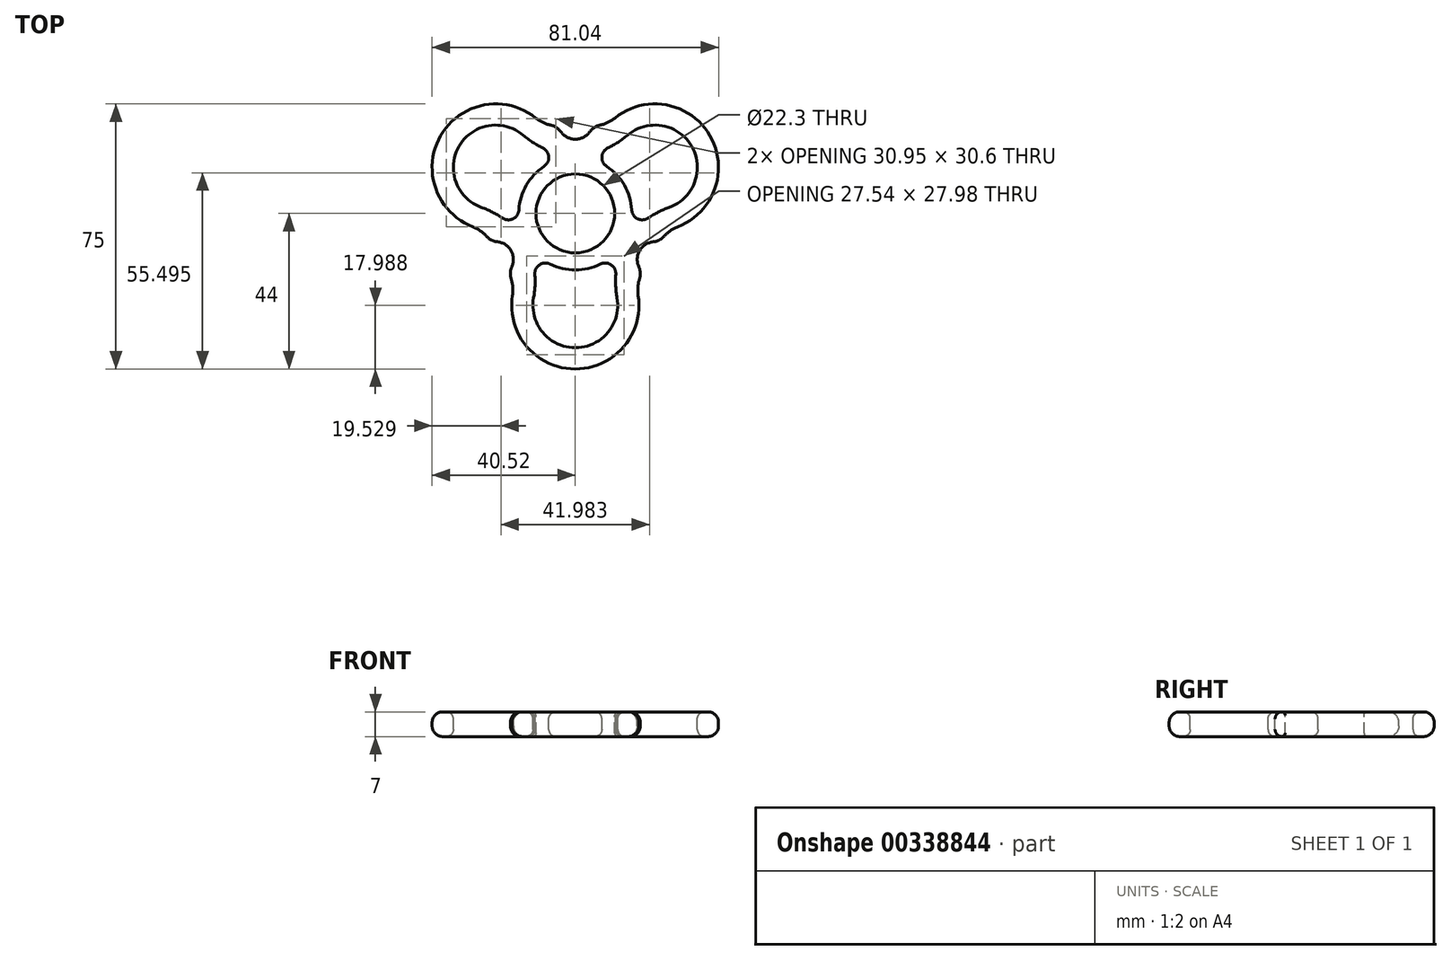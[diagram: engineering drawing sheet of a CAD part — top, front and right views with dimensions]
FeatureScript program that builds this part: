
annotation { "Feature Type Name" : "Feature", "Feature Type Description" : "" }
export const myFeature = defineFeature(function(context is Context, id is Id, definition is map)
    precondition{}
    {
        {
            var Q0;
            Q0=qCreatedBy(makeId("Top.planeOp"),FACE);
            var sketch = newSketch(context, id + "F0", { "sketchPlane" : qUnion([Q0])});
            skCircle(sketch, "E0.cCircle", {"center": v(0, 0) * mm, "radius": 22 * mm, "construction": true});
            skLineSegment(sketch, "E0.0", {"start": v(-38.1, 22) * mm, "end": v(38.1, 22) * mm});
            skLineSegment(sketch, "E0.1", {"start": v(38.1, 22) * mm, "end": v(0, -44) * mm});
            skLineSegment(sketch, "E0.2", {"start": v(0, -44) * mm, "end": v(-38.1, 22) * mm});
            skPoint(sketch, "E0.0.midPoint", {"position": v(0, 22) * mm});
            skLineSegment(sketch, "E1", {"start": v(-38.1, 22) * mm, "end": v(0, 26) * mm});
            skLineSegment(sketch, "E2", {"start": v(0, 26) * mm, "end": v(38.1, 22) * mm});
            skLineSegment(sketch, "E3.1.0", {"start": v(0, -44) * mm, "end": v(-22.52, -13) * mm});
            skLineSegment(sketch, "E3.1.1", {"start": v(-22.52, -13) * mm, "end": v(-38.1, 22) * mm});
            skLineSegment(sketch, "E3.2.0", {"start": v(38.1, 22) * mm, "end": v(22.52, -13) * mm});
            skLineSegment(sketch, "E3.2.1", {"start": v(22.52, -13) * mm, "end": v(0, -44) * mm});
            skSolve(sketch);
        }
        {
            var Q0;
            Q0=qSketchRegion(id+"F0",true);
            extrude(context, id + "F1", {"entities" : qUnion([Q0]), "depth" : 7 * mm});
        }
        {
            var Q0;
            Q0=makeQuery(id+"F1.opExtrude","CAP_FACE",FACE,{"disambiguationData":[OSD([sQuery(id+"F0.wireOp",EDGE,"E1"),sQuery(id+"F0.wireOp",EDGE,"E2"),sQuery(id+"F0.wireOp",EDGE,"E3.1.0"),sQuery(id+"F0.wireOp",EDGE,"E3.1.1"),sQuery(id+"F0.wireOp",EDGE,"E3.2.0"),sQuery(id+"F0.wireOp",EDGE,"E3.2.1")])],"isStart":true});
            var sketch = newSketch(context, id + "F2", { "sketchPlane" : qUnion([Q0])});
            skCircle(sketch, "E4", {"center": v(0, 0) * mm, "radius": 26 * mm, "construction": true});
            skLineSegment(sketch, "E5", {"start": v(0, 0) * mm, "end": v(-38.1, -22) * mm, "construction": true});
            skLineSegment(sketch, "E6", {"start": v(0, 0) * mm, "end": v(38.1, -22) * mm, "construction": true});
            skLineSegment(sketch, "E7", {"start": v(0, 0) * mm, "end": v(0, 44) * mm, "construction": true});
            skCircle(sketch, "E8", {"center": v(-22.52, -13) * mm, "radius": 18 * mm});
            skCircle(sketch, "E9", {"center": v(22.52, -13) * mm, "radius": 18 * mm});
            skCircle(sketch, "E10", {"center": v(0, 26) * mm, "radius": 18 * mm});
            skSolve(sketch);
        }
        {
            var Q0;
            Q0 = qSketchRegion(id + "F2", true);
            extrude(context, id + "F3", {"entities" : qUnion([Q0]), "operationType" : NewBodyOperationType.ADD, "oppositeDirection" : true, "depth" : 7 * mm});
        }
        {
            var Q0;
            Q0=makeQuery(id+"F1.opExtrude","CAP_FACE",FACE,{"disambiguationData":[OSD([sQuery(id+"F0.wireOp",EDGE,"E1"),sQuery(id+"F0.wireOp",EDGE,"E2"),sQuery(id+"F0.wireOp",EDGE,"E3.1.0"),sQuery(id+"F0.wireOp",EDGE,"E3.1.1"),sQuery(id+"F0.wireOp",EDGE,"E3.2.0"),sQuery(id+"F0.wireOp",EDGE,"E3.2.1")])],"isStart":false});
            var sketch = newSketch(context, id + "F4", { "sketchPlane" : qUnion([Q0])});
            skCircle(sketch, "E11", {"center": v(0, 0) * mm, "radius": 11.15 * mm});
            skSolve(sketch);
        }
        {
            var Q0;
            Q0=qSketchRegion(id+"F4",true);
            extrude(context, id + "F5", {"entities" : qUnion([Q0]), "operationType" : NewBodyOperationType.REMOVE, "endBound" : BoundingType.THROUGH_ALL, "oppositeDirection" : true, "depth" : 25 * mm});
        }
        {
            var Q0;
            Q0=makeQuery(id+"F1.opExtrude","CAP_FACE",FACE,{"disambiguationData":[OSD([sQuery(id+"F0.wireOp",EDGE,"E1"),sQuery(id+"F0.wireOp",EDGE,"E2"),sQuery(id+"F0.wireOp",EDGE,"E3.1.0"),sQuery(id+"F0.wireOp",EDGE,"E3.1.1"),sQuery(id+"F0.wireOp",EDGE,"E3.2.0"),sQuery(id+"F0.wireOp",EDGE,"E3.2.1")])],"isStart":false});
            var sketch = newSketch(context, id + "F6", { "sketchPlane" : qUnion([Q0])});
            skArc(sketch, "E12", {"start": v(-4.05, 23.06) * mm, "mid": v(0, 21) * mm, "end": v(4.05, 23.06) * mm});
            skLineSegment(sketch, "E13", {"start": v(-31.26, 22.72) * mm, "end": v(-8.61, 25.1) * mm});
            skLineSegment(sketch, "E14", {"start": v(8.61, 25.1) * mm, "end": v(31.26, 22.72) * mm});
            skPoint(sketch, "E15.visualSharp", {"position": v(-4.97, 25.48) * mm});
            skArc(sketch, "E15.filletArc", {"start": v(-4.05, 23.06) * mm, "mid": v(-6.06, 24.7) * mm, "end": v(-8.61, 25.1) * mm});
            skPoint(sketch, "E16.visualSharp", {"position": v(4.97, 25.48) * mm});
            skArc(sketch, "E16.filletArc", {"start": v(8.61, 25.1) * mm, "mid": v(6.06, 24.7) * mm, "end": v(4.05, 23.06) * mm});
            skLineSegment(sketch, "E17", {"start": v(-8.61, 25.1) * mm, "end": v(0, 26) * mm});
            skLineSegment(sketch, "E18", {"start": v(8.61, 25.1) * mm, "end": v(0, 26) * mm});
            skLineSegment(sketch, "E19.1.0", {"start": v(-4.05, -38.43) * mm, "end": v(-17.43, -20) * mm});
            skLineSegment(sketch, "E19.1.1", {"start": v(-26.04, -5.09) * mm, "end": v(-35.3, 15.71) * mm});
            skPoint(sketch, "E19.1.2", {"position": v(-24.55, -8.43) * mm});
            skLineSegment(sketch, "E19.1.3", {"start": v(-17.43, -20) * mm, "end": v(-22.52, -13) * mm});
            skLineSegment(sketch, "E19.1.4", {"start": v(-26.04, -5.09) * mm, "end": v(-22.52, -13) * mm});
            skPoint(sketch, "E19.1.5", {"position": v(-19.58, -17.05) * mm});
            skArc(sketch, "E19.1.6", {"start": v(-17.95, -15.03) * mm, "mid": v(-18.19, -10.5) * mm, "end": v(-22, -8.03) * mm});
            skArc(sketch, "E19.1.7", {"start": v(-17.95, -15.03) * mm, "mid": v(-18.35, -17.6) * mm, "end": v(-17.43, -20) * mm});
            skArc(sketch, "E19.1.8", {"start": v(-26.04, -5.09) * mm, "mid": v(-24.41, -7.1) * mm, "end": v(-22, -8.03) * mm});
            skLineSegment(sketch, "E19.2.0", {"start": v(35.3, 15.71) * mm, "end": v(26.04, -5.09) * mm});
            skLineSegment(sketch, "E19.2.1", {"start": v(17.43, -20) * mm, "end": v(4.05, -38.43) * mm});
            skPoint(sketch, "E19.2.2", {"position": v(19.58, -17.05) * mm});
            skLineSegment(sketch, "E19.2.3", {"start": v(26.04, -5.09) * mm, "end": v(22.52, -13) * mm});
            skLineSegment(sketch, "E19.2.4", {"start": v(17.43, -20) * mm, "end": v(22.52, -13) * mm});
            skPoint(sketch, "E19.2.5", {"position": v(24.55, -8.43) * mm});
            skArc(sketch, "E19.2.6", {"start": v(22, -8.03) * mm, "mid": v(18.19, -10.5) * mm, "end": v(17.95, -15.03) * mm});
            skArc(sketch, "E19.2.7", {"start": v(22, -8.03) * mm, "mid": v(24.41, -7.1) * mm, "end": v(26.04, -5.09) * mm});
            skArc(sketch, "E19.2.8", {"start": v(17.43, -20) * mm, "mid": v(18.35, -17.6) * mm, "end": v(17.95, -15.03) * mm});
            skPoint(sketch, "E19.center", {"position": v(0, 0) * mm});
            skSolve(sketch);
        }
        {
            var Q0;
            Q0=qSketchRegion(id+"F6",true);
            extrude(context, id + "F7", {"entities" : qUnion([Q0]), "operationType" : NewBodyOperationType.REMOVE, "endBound" : BoundingType.THROUGH_ALL, "oppositeDirection" : true, "depth" : 25 * mm});
        }
        {
            var Q0;
            Q0=makeQuery(id+"F5.boolean.opBoolean","COPY",FACE,{"derivedFrom":makeQuery(id+"F5.opExtrude","SWEPT_FACE",FACE,{"disambiguationData":[OSD([sQuery(id+"F4.wireOp",EDGE,"E11")])]})});
            fillet(context, id + "F8", {"entities" : qUnion([Q0]), "radius" : 1 * mm, "tangentPropagation" : true, "allowEdgeOverflow" : false});
        }
        {
            var Q0;
            Q0=makeQuery(id+"F3.boolean.opBoolean","INTERSECT",EDGE,{"derivedFrom":[makeQuery(id+"F1.opExtrude","SWEPT_FACE",FACE,{"disambiguationData":[OSD([sQuery(id+"F0.wireOp",EDGE,"E3.2.0")])]}),makeQuery(id+"F3.opExtrude","SWEPT_FACE",FACE,{"disambiguationData":[OSD([sQuery(id+"F2.wireOp",EDGE,"E9")])]})]});
            var Q1;
            Q1=makeQuery(id+"F1.opExtrude","SWEPT_EDGE",EDGE,{"disambiguationData":[OSD([sQuery(id+"F0.wireOp",EDGE,"E3.2.0"),sQuery(id+"F0.wireOp",EDGE,"E3.2.1")])]});
            var Q2;
            Q2=makeQuery(id+"F3.boolean.opBoolean","INTERSECT",EDGE,{"derivedFrom":[makeQuery(id+"F1.opExtrude","SWEPT_FACE",FACE,{"disambiguationData":[OSD([sQuery(id+"F0.wireOp",EDGE,"E3.2.1")])]}),makeQuery(id+"F3.opExtrude","SWEPT_FACE",FACE,{"disambiguationData":[OSD([sQuery(id+"F2.wireOp",EDGE,"E10")])]})]});
            var Q3;
            Q3=makeQuery(id+"F3.boolean.opBoolean","INTERSECT",EDGE,{"derivedFrom":[makeQuery(id+"F1.opExtrude","SWEPT_FACE",FACE,{"disambiguationData":[OSD([sQuery(id+"F0.wireOp",EDGE,"E3.1.0")])]}),makeQuery(id+"F3.opExtrude","SWEPT_FACE",FACE,{"disambiguationData":[OSD([sQuery(id+"F2.wireOp",EDGE,"E10")])]})]});
            var Q4;
            Q4=makeQuery(id+"F1.opExtrude","SWEPT_EDGE",EDGE,{"disambiguationData":[OSD([sQuery(id+"F0.wireOp",EDGE,"E3.1.0"),sQuery(id+"F0.wireOp",EDGE,"E3.1.1")])]});
            var Q5;
            Q5=makeQuery(id+"F3.boolean.opBoolean","INTERSECT",EDGE,{"derivedFrom":[makeQuery(id+"F1.opExtrude","SWEPT_FACE",FACE,{"disambiguationData":[OSD([sQuery(id+"F0.wireOp",EDGE,"E3.1.1")])]}),makeQuery(id+"F3.opExtrude","SWEPT_FACE",FACE,{"disambiguationData":[OSD([sQuery(id+"F2.wireOp",EDGE,"E8")])]})]});
            var Q6;
            Q6=makeQuery(id+"F3.boolean.opBoolean","INTERSECT",EDGE,{"derivedFrom":[makeQuery(id+"F1.opExtrude","SWEPT_FACE",FACE,{"disambiguationData":[OSD([sQuery(id+"F0.wireOp",EDGE,"E1")])]}),makeQuery(id+"F3.opExtrude","SWEPT_FACE",FACE,{"disambiguationData":[OSD([sQuery(id+"F2.wireOp",EDGE,"E8")])]})]});
            var Q7;
            Q7=makeQuery(id+"F1.opExtrude","SWEPT_EDGE",EDGE,{"disambiguationData":[OSD([sQuery(id+"F0.wireOp",EDGE,"E1"),sQuery(id+"F0.wireOp",EDGE,"E2")])]});
            var Q8;
            Q8=makeQuery(id+"F3.boolean.opBoolean","INTERSECT",EDGE,{"derivedFrom":[makeQuery(id+"F1.opExtrude","SWEPT_FACE",FACE,{"disambiguationData":[OSD([sQuery(id+"F0.wireOp",EDGE,"E2")])]}),makeQuery(id+"F3.opExtrude","SWEPT_FACE",FACE,{"disambiguationData":[OSD([sQuery(id+"F2.wireOp",EDGE,"E9")])]})]});
            fillet(context, id + "F9", {"entities" : qUnion([Q0, Q1, Q2, Q3, Q4, Q5, Q6, Q7, Q8]), "radius" : 10 * mm, "tangentPropagation" : true, "allowEdgeOverflow" : false});
        }
        {
            var Q0;
            Q0=makeQuery(id+"F3.boolean.opBoolean","MERGE",FACE,{"derivedFrom":[makeQuery(id+"F1.opExtrude","CAP_FACE",FACE,{"disambiguationData":[OSD([sQuery(id+"F0.wireOp",EDGE,"E1"),sQuery(id+"F0.wireOp",EDGE,"E2"),sQuery(id+"F0.wireOp",EDGE,"E3.1.0"),sQuery(id+"F0.wireOp",EDGE,"E3.1.1"),sQuery(id+"F0.wireOp",EDGE,"E3.2.0"),sQuery(id+"F0.wireOp",EDGE,"E3.2.1")])],"isStart":true}),makeQuery(id+"F3.opExtrude","CAP_FACE",FACE,{"disambiguationData":[OSD([sQuery(id+"F2.wireOp",EDGE,"E8")])],"isStart":true}),makeQuery(id+"F3.opExtrude","CAP_FACE",FACE,{"disambiguationData":[OSD([sQuery(id+"F2.wireOp",EDGE,"E9")])],"isStart":true}),makeQuery(id+"F3.opExtrude","CAP_FACE",FACE,{"disambiguationData":[OSD([sQuery(id+"F2.wireOp",EDGE,"E10")])],"isStart":true})]});
            var Q1;
            Q1=makeQuery(id+"F3.boolean.opBoolean","MERGE",FACE,{"derivedFrom":[makeQuery(id+"F1.opExtrude","CAP_FACE",FACE,{"disambiguationData":[OSD([sQuery(id+"F0.wireOp",EDGE,"E1"),sQuery(id+"F0.wireOp",EDGE,"E2"),sQuery(id+"F0.wireOp",EDGE,"E3.1.0"),sQuery(id+"F0.wireOp",EDGE,"E3.1.1"),sQuery(id+"F0.wireOp",EDGE,"E3.2.0"),sQuery(id+"F0.wireOp",EDGE,"E3.2.1")])],"isStart":false}),makeQuery(id+"F3.opExtrude","CAP_FACE",FACE,{"disambiguationData":[OSD([sQuery(id+"F2.wireOp",EDGE,"E8")])],"isStart":false}),makeQuery(id+"F3.opExtrude","CAP_FACE",FACE,{"disambiguationData":[OSD([sQuery(id+"F2.wireOp",EDGE,"E9")])],"isStart":false}),makeQuery(id+"F3.opExtrude","CAP_FACE",FACE,{"disambiguationData":[OSD([sQuery(id+"F2.wireOp",EDGE,"E10")])],"isStart":false})]});
            fillet(context, id + "F10", {"entities" : qUnion([Q0, Q1]), "radius" : 3 * mm, "tangentPropagation" : true, "allowEdgeOverflow" : false});
        }
        {
            var Q0;
            Q0=makeQuery(id+"F3.boolean.opBoolean","MERGE",FACE,{"derivedFrom":[makeQuery(id+"F1.opExtrude","CAP_FACE",FACE,{"disambiguationData":[OSD([sQuery(id+"F0.wireOp",EDGE,"E1"),sQuery(id+"F0.wireOp",EDGE,"E2"),sQuery(id+"F0.wireOp",EDGE,"E3.1.0"),sQuery(id+"F0.wireOp",EDGE,"E3.1.1"),sQuery(id+"F0.wireOp",EDGE,"E3.2.0"),sQuery(id+"F0.wireOp",EDGE,"E3.2.1")])],"isStart":false}),makeQuery(id+"F3.opExtrude","CAP_FACE",FACE,{"disambiguationData":[OSD([sQuery(id+"F2.wireOp",EDGE,"E8")])],"isStart":false}),makeQuery(id+"F3.opExtrude","CAP_FACE",FACE,{"disambiguationData":[OSD([sQuery(id+"F2.wireOp",EDGE,"E9")])],"isStart":false}),makeQuery(id+"F3.opExtrude","CAP_FACE",FACE,{"disambiguationData":[OSD([sQuery(id+"F2.wireOp",EDGE,"E10")])],"isStart":false})]});
            var sketch = newSketch(context, id + "F11", { "sketchPlane" : qUnion([Q0])});
            skArc(sketch, "E20", {"start": v(-7.12, -14.33) * mm, "mid": v(0, -16) * mm, "end": v(7.12, -14.33) * mm});
            skArc(sketch, "E21", {"start": v(-11.8, -23.84) * mm, "mid": v(0, -38) * mm, "end": v(11.8, -23.84) * mm});
            skArc(sketch, "E22", {"start": v(-11.8, -23.84) * mm, "mid": v(-11.42, -20.55) * mm, "end": v(-11.45, -17.24) * mm});
            skArc(sketch, "E23", {"start": v(11.45, -17.24) * mm, "mid": v(11.42, -20.55) * mm, "end": v(11.8, -23.84) * mm});
            skPoint(sketch, "E24.visualSharp", {"position": v(-14.24, -7.3) * mm});
            skArc(sketch, "E24.filletArc", {"start": v(-7.12, -14.33) * mm, "mid": v(-10.13, -14.52) * mm, "end": v(-11.45, -17.24) * mm});
            skPoint(sketch, "E25.visualSharp", {"position": v(14.24, -7.3) * mm});
            skArc(sketch, "E25.filletArc", {"start": v(11.45, -17.24) * mm, "mid": v(10.13, -14.52) * mm, "end": v(7.12, -14.33) * mm});
            skArc(sketch, "E26.1.0", {"start": v(15.97, 1) * mm, "mid": v(13.86, 8) * mm, "end": v(8.85, 13.33) * mm});
            skArc(sketch, "E26.1.1", {"start": v(26.55, 1.7) * mm, "mid": v(32.9, 19) * mm, "end": v(14.74, 22.14) * mm});
            skArc(sketch, "E26.1.2", {"start": v(26.55, 1.7) * mm, "mid": v(23.5, 0.39) * mm, "end": v(20.65, -1.3) * mm});
            skArc(sketch, "E26.1.3", {"start": v(9.2, 18.53) * mm, "mid": v(7.51, 16.04) * mm, "end": v(8.85, 13.33) * mm});
            skArc(sketch, "E26.1.4", {"start": v(15.97, 1) * mm, "mid": v(17.64, -1.51) * mm, "end": v(20.65, -1.3) * mm});
            skArc(sketch, "E26.1.5", {"start": v(9.2, 18.53) * mm, "mid": v(12.09, 20.16) * mm, "end": v(14.74, 22.14) * mm});
            skArc(sketch, "E26.2.0", {"start": v(-8.85, 13.33) * mm, "mid": v(-13.86, 8) * mm, "end": v(-15.97, 1) * mm});
            skArc(sketch, "E26.2.1", {"start": v(-14.74, 22.14) * mm, "mid": v(-32.9, 19) * mm, "end": v(-26.55, 1.7) * mm});
            skArc(sketch, "E26.2.2", {"start": v(-14.74, 22.14) * mm, "mid": v(-12.09, 20.16) * mm, "end": v(-9.2, 18.53) * mm});
            skArc(sketch, "E26.2.3", {"start": v(-20.65, -1.3) * mm, "mid": v(-17.64, -1.51) * mm, "end": v(-15.97, 1) * mm});
            skArc(sketch, "E26.2.4", {"start": v(-8.85, 13.33) * mm, "mid": v(-7.51, 16.04) * mm, "end": v(-9.2, 18.53) * mm});
            skArc(sketch, "E26.2.5", {"start": v(-20.65, -1.3) * mm, "mid": v(-23.5, 0.39) * mm, "end": v(-26.55, 1.7) * mm});
            skSolve(sketch);
        }
        {
            var Q0;
            Q0 = qSketchRegion(id + "F11", true);
            extrude(context, id + "F12", {"entities" : qUnion([Q0]), "operationType" : NewBodyOperationType.REMOVE, "endBound" : BoundingType.THROUGH_ALL, "oppositeDirection" : true, "depth" : 25 * mm});
        }
        {
            var Q0;
            Q0=makeQuery(id+"F3.boolean.opBoolean","MERGE",FACE,{"derivedFrom":[makeQuery(id+"F1.opExtrude","CAP_FACE",FACE,{"disambiguationData":[OSD([sQuery(id+"F0.wireOp",EDGE,"E1"),sQuery(id+"F0.wireOp",EDGE,"E2"),sQuery(id+"F0.wireOp",EDGE,"E3.1.0"),sQuery(id+"F0.wireOp",EDGE,"E3.1.1"),sQuery(id+"F0.wireOp",EDGE,"E3.2.0"),sQuery(id+"F0.wireOp",EDGE,"E3.2.1")])],"isStart":false}),makeQuery(id+"F3.opExtrude","CAP_FACE",FACE,{"disambiguationData":[OSD([sQuery(id+"F2.wireOp",EDGE,"E8")])],"isStart":false}),makeQuery(id+"F3.opExtrude","CAP_FACE",FACE,{"disambiguationData":[OSD([sQuery(id+"F2.wireOp",EDGE,"E9")])],"isStart":false}),makeQuery(id+"F3.opExtrude","CAP_FACE",FACE,{"disambiguationData":[OSD([sQuery(id+"F2.wireOp",EDGE,"E10")])],"isStart":false})]});
            var Q1;
            Q1=makeQuery(id+"F3.boolean.opBoolean","MERGE",FACE,{"derivedFrom":[makeQuery(id+"F1.opExtrude","CAP_FACE",FACE,{"disambiguationData":[OSD([sQuery(id+"F0.wireOp",EDGE,"E1"),sQuery(id+"F0.wireOp",EDGE,"E2"),sQuery(id+"F0.wireOp",EDGE,"E3.1.0"),sQuery(id+"F0.wireOp",EDGE,"E3.1.1"),sQuery(id+"F0.wireOp",EDGE,"E3.2.0"),sQuery(id+"F0.wireOp",EDGE,"E3.2.1")])],"isStart":true}),makeQuery(id+"F3.opExtrude","CAP_FACE",FACE,{"disambiguationData":[OSD([sQuery(id+"F2.wireOp",EDGE,"E8")])],"isStart":true}),makeQuery(id+"F3.opExtrude","CAP_FACE",FACE,{"disambiguationData":[OSD([sQuery(id+"F2.wireOp",EDGE,"E9")])],"isStart":true}),makeQuery(id+"F3.opExtrude","CAP_FACE",FACE,{"disambiguationData":[OSD([sQuery(id+"F2.wireOp",EDGE,"E10")])],"isStart":true})]});
            fillet(context, id + "F13", {"entities" : qUnion([Q0, Q1]), "radius" : 2 * mm, "tangentPropagation" : true, "allowEdgeOverflow" : false});
        }
    });
